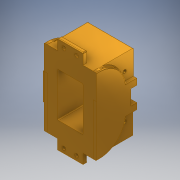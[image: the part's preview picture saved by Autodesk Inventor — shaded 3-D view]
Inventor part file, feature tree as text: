
AUTODESK INVENTOR PART (.ipt)
format: ipt  version: 2017 (Build 210142000, 142)  size: 615,424 bytes
history: native  units: mm
features: extrude x13, sketch x13, projected_geometry x8, plane x3, mirror x3, fillet x2
ambient origin geometry x8: Origin, YZ Plane, XZ Plane, XY Plane, X Axis, Y Axis, Z Axis, Center Point
bodies: Solid1 (feature_tree)
feature tree (42):
  extrude  "Extrusion1"  Depth=54.0mm
  extrude  "Extrusion2"  Depth=54.0mm
  extrude  "Extrusion3"  Depth=5.0mm
  plane  "Work Plane1"
  mirror  "Mirror2"
  mirror  "Mirror3"
  extrude  "Extrusion4"  Depth=4.5mm
  extrude  "Extrusion5"  Depth=6.25mm
  extrude  "Extrusion7"  TaperAngle=90.0deg  [1 undecoded]
  extrude  "Extrusion8"  Depth=25.0mm
  extrude  "Extrusion9"  Depth=30.0mm
  extrude  "Extrusion10"  Depth=7.5mm
  extrude  "Extrusion11"  Depth=12.5mm TaperAngle=0.0deg
  extrude  "Extrusion13"  Depth=4.0mm TaperAngle=0.0deg
  plane  "Work Plane3"
  mirror  "Mirror4"
  extrude  "Extrusion14"  Depth=0.000366mm
  fillet  "Fillet1"  Radius=60.705711mm
  extrude  "Extrusion15"  Depth=1.0mm TaperAngle=0.0deg
  fillet  "Fillet2"  Radius=7.0mm
  sketch  "Sketch2"  dims[d4=90.0mm d5=54.0mm]
  sketch  "Sketch3"  dims[d6=90.0mm d7=54.0mm]
  sketch  "Sketch5"  dims[d8=47.5mm d9=0.0mm d10=5.0mm d11=30.0mm]
  projected_geometry  "Projected Loop1"
  plane  "Work Plane2"
  sketch  "Sketch6"  dims[d12=12.5mm d13=0.0mm d14=4.5mm d15=4.5mm]
  sketch  "Sketch7"  dims[d16=6.25mm d17=6.25mm]
  sketch  "Sketch11"  dims[d18=15.0mm d19=90.0deg]
  sketch  "Sketch12"  dims[d20=90.0deg d21=25.0mm]
  sketch  "Sketch15"  dims[d22=0.0mm d23=30.0mm]
  projected_geometry  "Projected Loop3"
  projected_geometry  "Projected Loop4"
  sketch  "Sketch16"  dims[d24=12.5mm d25=7.5mm]
  projected_geometry  "Projected Loop5"
  sketch  "Sketch17"  dims[d26=12.5mm d27=12.5mm d28=0.0mm]
  projected_geometry  "Projected Loop6"
  projected_geometry  "Projected Loop7"
  sketch  "Sketch18"  dims[d29=45.0mm d35=4.0mm d36=0.0mm]
  sketch  "Sketch19"  dims[d37=47.5mm d38=32.0mm d39=0.000366mm d40=60.705711mm]
  sketch  "Sketch20"  dims[d41=0.001172mm d42=4.0mm d43=0.0mm d45=7.0mm d46=47.5mm d47=7.0mm d48=47.5mm d55=46.0mm d56=58.0mm d59=18.0mm d62=58.0mm d66=16.0mm d67=18.0mm d68=16.0mm d69=16.0mm d70=18.0mm d71=7.0mm d72=0.0mm d73=26.0mm d74=26.0mm d75=30.0mm d76=16.0mm d77=19.0mm d78=52.0mm d79=90.0deg d80=36.0mm d81=58.0mm d82=0.0mm d83=0.0mm d84=0.0mm d85=2.5mm d86=12.0mm d87=3.5mm d88=2.5mm d89=3.2mm d90=4.0mm d97=2.5mm d98=4.1mm d99=3.5mm d100=2.3mm d101=3.5mm d102=11.0mm d103=2.5mm d106=2.5mm d107=3.5mm d108=2.5mm d109=3.2mm d110=2.5mm d111=2.5mm d112=3.5mm d113=6.9mm d114=2.5mm d115=5.5mm d117=54.0mm d118=8.0mm d119=0.0mm d120=8.0mm d121=8.0mm d122=16.0mm d123=6.0mm d124=19.0mm d125=8.0mm d126=8.0mm d127=16.0mm d130=6.0mm d131=19.0mm d132=23.0mm d133=23.0mm d134=58.0mm d135=0.0mm d136=8.0mm d137=0.0mm d138=90.0deg d139=1.396263mm d140=90.0deg d141=15.787291mm d142=1.396263mm d143=14.717306mm d144=75.352856mm d145=3.000844mm d146=0.0mm d147=6.610722mm d148=0.0mm d149=3.664235mm d150=82.513404mm d151=72.352856mm d152=4.0mm d153=0.0mm d154=31.546191mm d155=34.84835mm d156=34.847179mm d157=31.546mm d158=31.415523mm d159=0.001172mm d160=32.0mm d161=0.002969mm d162=19.479459mm d163=0.0mm d164=0.0mm d167=4.0mm d168=0.0mm d169=27.0mm d170=1.0mm d171=0.0mm d172=1.0mm d173=4.0mm d174=33.8mm d175=19.0mm d176=4.0mm d177=18.5mm d180=33.8mm d181=20.0mm d182=0.0mm d183=1.0mm]
  projected_geometry  "Projected Loop8"
  projected_geometry  "Projected Loop9"
note: 1 required parameter value undecoded (feature->parameter linkage not recoverable at this tier; creation-order binding heuristic only, values carry confidence <= 0.55)
